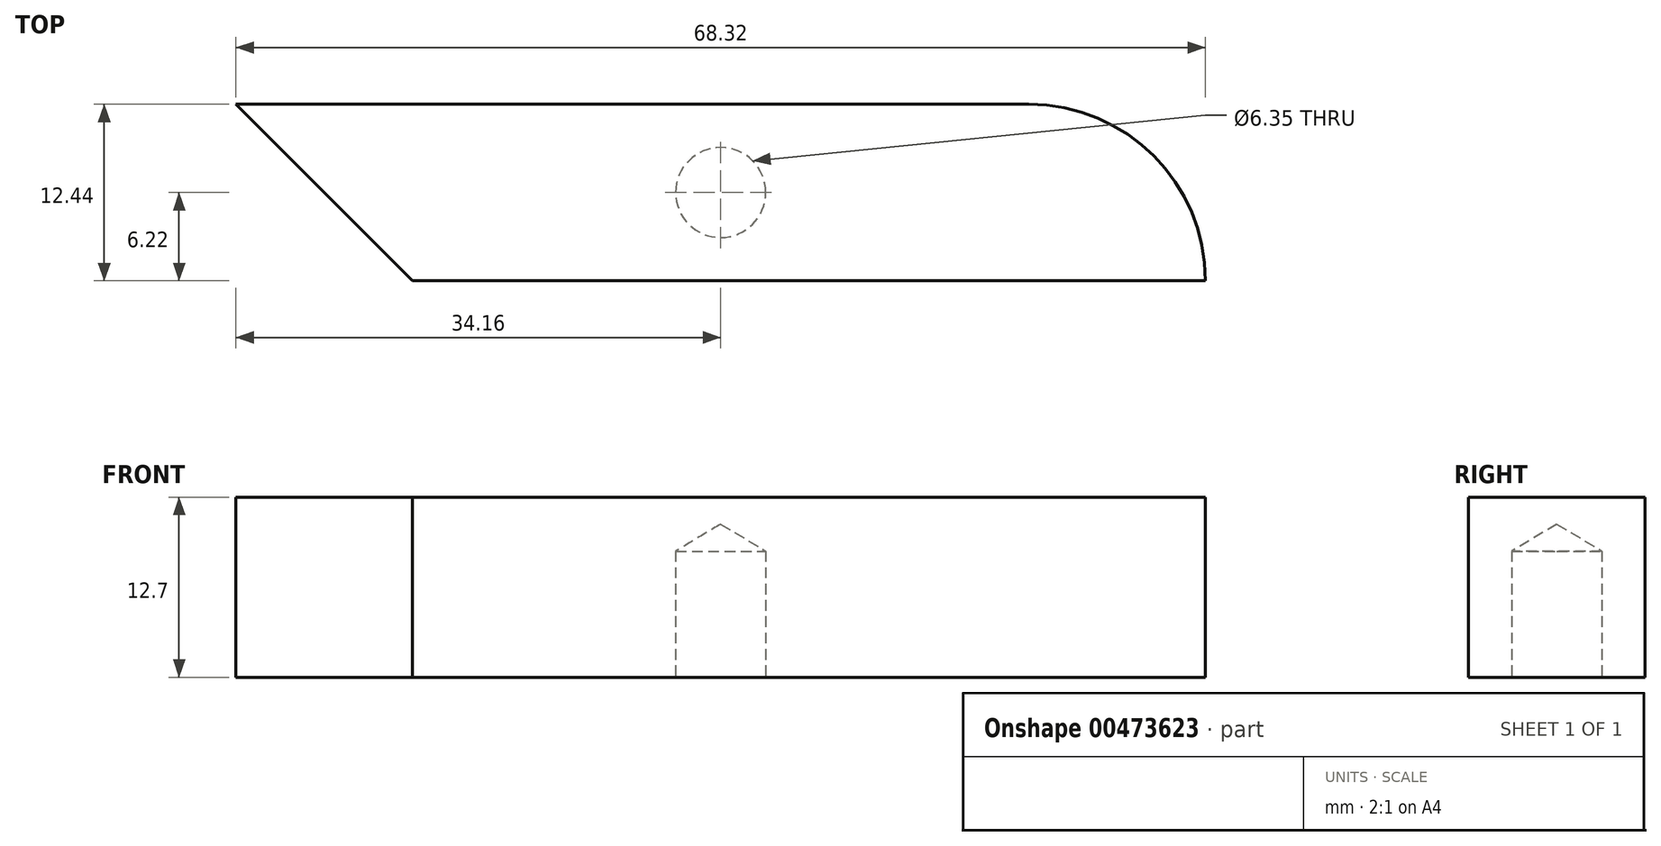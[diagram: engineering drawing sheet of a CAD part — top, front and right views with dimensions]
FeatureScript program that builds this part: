
annotation { "Feature Type Name" : "Feature", "Feature Type Description" : "" }
export const myFeature = defineFeature(function(context is Context, id is Id, definition is map)
    precondition{}
    {
        {
            var Q0;
            Q0=qCreatedBy(makeId("Top.planeOp"),FACE);
            var sketch = newSketch(context, id + "F0", { "sketchPlane" : qUnion([Q0])});
            skLineSegment(sketch, "E0.bottom", {"start": v(34.16, 6.22) * mm, "end": v(-34.16, 6.22) * mm});
            skLineSegment(sketch, "E0.top", {"start": v(34.16, -6.22) * mm, "end": v(-34.16, -6.22) * mm});
            skLineSegment(sketch, "E0.left", {"start": v(34.16, 6.22) * mm, "end": v(34.16, -6.22) * mm});
            skLineSegment(sketch, "E0.right", {"start": v(-34.16, 6.22) * mm, "end": v(-34.16, -6.22) * mm});
            skPoint(sketch, "E0.middle", {"position": v(0, 0) * mm});
            skSolve(sketch);
        }
        {
            var Q0;
            Q0=makeQuery(id+"F0.imprint","IMPRINT",FACE,{"disambiguationData":[TD([[makeQuery(id+"F0.imprint","IMPRINT",EDGE,{"derivedFrom":sQuery(id+"F0.wireOp",EDGE,"E0.bottom")}),1.0]])]});
            extrude(context, id + "F1", {"entities" : qUnion([Q0]), "depth" : 12.7 * mm});
        }
        {
            var Q0;
            Q0=makeQuery(id+"F1.opExtrude","SWEPT_EDGE",EDGE,{"disambiguationData":[OSD([sQuery(id+"F0.wireOp",EDGE,"E0.top"),sQuery(id+"F0.wireOp",EDGE,"E0.right")])]});
            chamfer(context, id + "F2", {"entities" : qUnion([Q0]), "width" : 12.45 * mm, "tangentPropagation" : true});
        }
        {
            var Q0;
            Q0=makeQuery(id+"F1.opExtrude","SWEPT_EDGE",EDGE,{"disambiguationData":[OSD([sQuery(id+"F0.wireOp",EDGE,"E0.bottom"),sQuery(id+"F0.wireOp",EDGE,"E0.left")])]});
            fillet(context, id + "F3", {"entities" : qUnion([Q0]), "radius" : 12.45 * mm, "tangentPropagation" : true, "allowEdgeOverflow" : false});
        }
        {
            var Q0;
            Q0=makeQuery(id+"F1.opExtrude","CAP_FACE",FACE,{"disambiguationData":[OSD([sQuery(id+"F0.wireOp",EDGE,"E0.bottom"),sQuery(id+"F0.wireOp",EDGE,"E0.top"),sQuery(id+"F0.wireOp",EDGE,"E0.left"),sQuery(id+"F0.wireOp",EDGE,"E0.right")])],"isStart":true});
            var sketch = newSketch(context, id + "F4", { "sketchPlane" : qUnion([Q0])});
            skPoint(sketch, "E1", {"position": v(0, 0) * mm});
            skSolve(sketch);
        }
        {
            var Q0;
            Q0=sQuery(id+"F4.wireOp",VERTEX,"E1");
            var Q1;
            Q1=makeQuery(id+"F1.opExtrude","SWEPT_BODY",BODY,{"disambiguationData":[OSD([sQuery(id+"F0.wireOp",EDGE,"E0.bottom"),sQuery(id+"F0.wireOp",EDGE,"E0.top"),sQuery(id+"F0.wireOp",EDGE,"E0.left"),sQuery(id+"F0.wireOp",EDGE,"E0.right")])]});
            hole(context, id + "F5", {"style" : HoleStyle.SIMPLE, "endStyle" : HoleEndStyle.BLIND, "holeDiameter" : 6.35 * mm, "holeDepth" : 8.9 * mm, "isTappedThrough" : true, "tappedDepth" : 12.7 * mm, "tapClearance" : 3, "locations" : qUnion([Q0]), "scope" : qUnion([Q1])});
        }
    });
